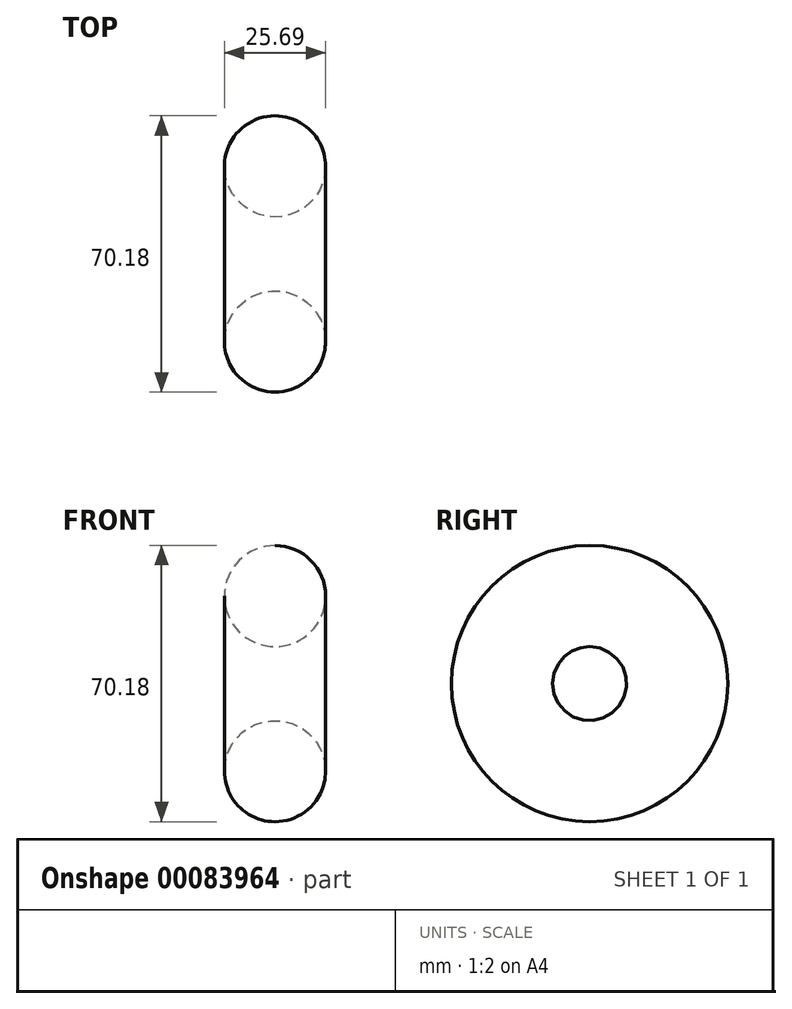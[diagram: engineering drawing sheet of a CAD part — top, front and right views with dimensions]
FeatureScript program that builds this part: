
annotation { "Feature Type Name" : "Feature", "Feature Type Description" : "" }
export const myFeature = defineFeature(function(context is Context, id is Id, definition is map)
    precondition{}
    {
        {
            var Q0;
            Q0=qCreatedBy(makeId("Top.planeOp"),FACE);
            var sketch = newSketch(context, id + "F0", { "sketchPlane" : qUnion([Q0])});
            skCircle(sketch, "E0", {"center": v(23.32, 28.66) * mm, "radius": 12.85 * mm});
            skLineSegment(sketch, "E1", {"start": v(15.55, 6.42) * mm, "end": v(32.73, 6.42) * mm, "construction": true});
            skSolve(sketch);
        }
        {
            var Q0;
            Q0=makeQuery(id+"F0.imprint","IMPRINT",FACE,{"disambiguationData":[TD([[makeQuery(id+"F0.imprint","IMPRINT",EDGE,{"derivedFrom":sQuery(id+"F0.wireOp",EDGE,"E0")}),1.0]])]});
            var Q1;
            Q1=sQuery(id+"F0.wireOp",EDGE,"E1");
            revolve(context, id + "F1", {"entities" : qUnion([Q0]), "axis" : qUnion([Q1]), "revolveType" : RevolveType.FULL});
        }
    });
